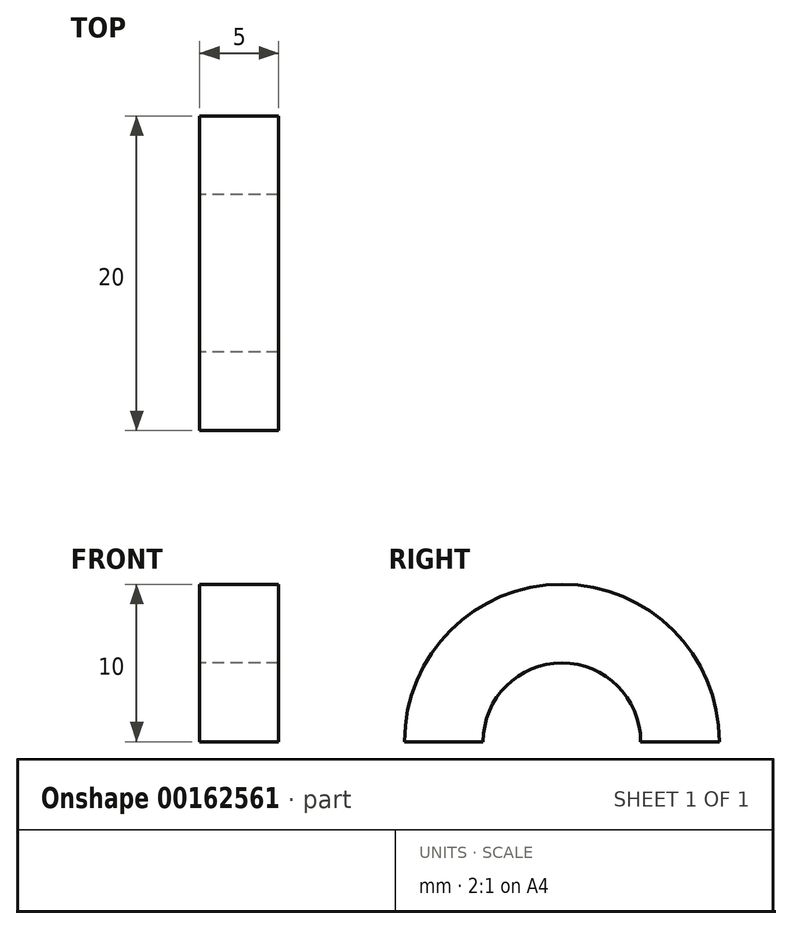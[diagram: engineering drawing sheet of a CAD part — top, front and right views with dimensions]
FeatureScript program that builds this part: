
annotation { "Feature Type Name" : "Feature", "Feature Type Description" : "" }
export const myFeature = defineFeature(function(context is Context, id is Id, definition is map)
    precondition{}
    {
        {
            var Q0;
            Q0=qCreatedBy(makeId("Top.planeOp"),FACE);
            var sketch = newSketch(context, id + "F0", { "sketchPlane" : qUnion([Q0])});
            skLineSegment(sketch, "E0.bottom", {"start": v(0, -5) * mm, "end": v(-5, -5) * mm});
            skLineSegment(sketch, "E0.top", {"start": v(0, -10) * mm, "end": v(-5, -10) * mm});
            skLineSegment(sketch, "E0.left", {"start": v(0, -5) * mm, "end": v(0, -10) * mm});
            skLineSegment(sketch, "E0.right", {"start": v(-5, -5) * mm, "end": v(-5, -10) * mm});
            skSolve(sketch);
        }
        {
            var Q0;
            Q0=qCreatedBy(makeId("Right.planeOp"),FACE);
            var sketch = newSketch(context, id + "F1", { "sketchPlane" : qUnion([Q0])});
            skArc(sketch, "E1", {"start": v(-5.05, 0) * mm, "mid": v(0, 5.05) * mm, "end": v(5.05, 0) * mm});
            skSolve(sketch);
        }
        {
            var Q0;
            Q0 = qSketchRegion(id + "F0", true);
            var Q1;
            Q1 = qConstructionFilter(qBodyType(qCreatedBy(id + "F1" ,EDGE), BodyType.WIRE), ConstructionObject.NO);
            sweep(context, id + "F2", {"profiles" : qUnion([Q0]), "path" : qUnion([Q1])});
        }
    });
